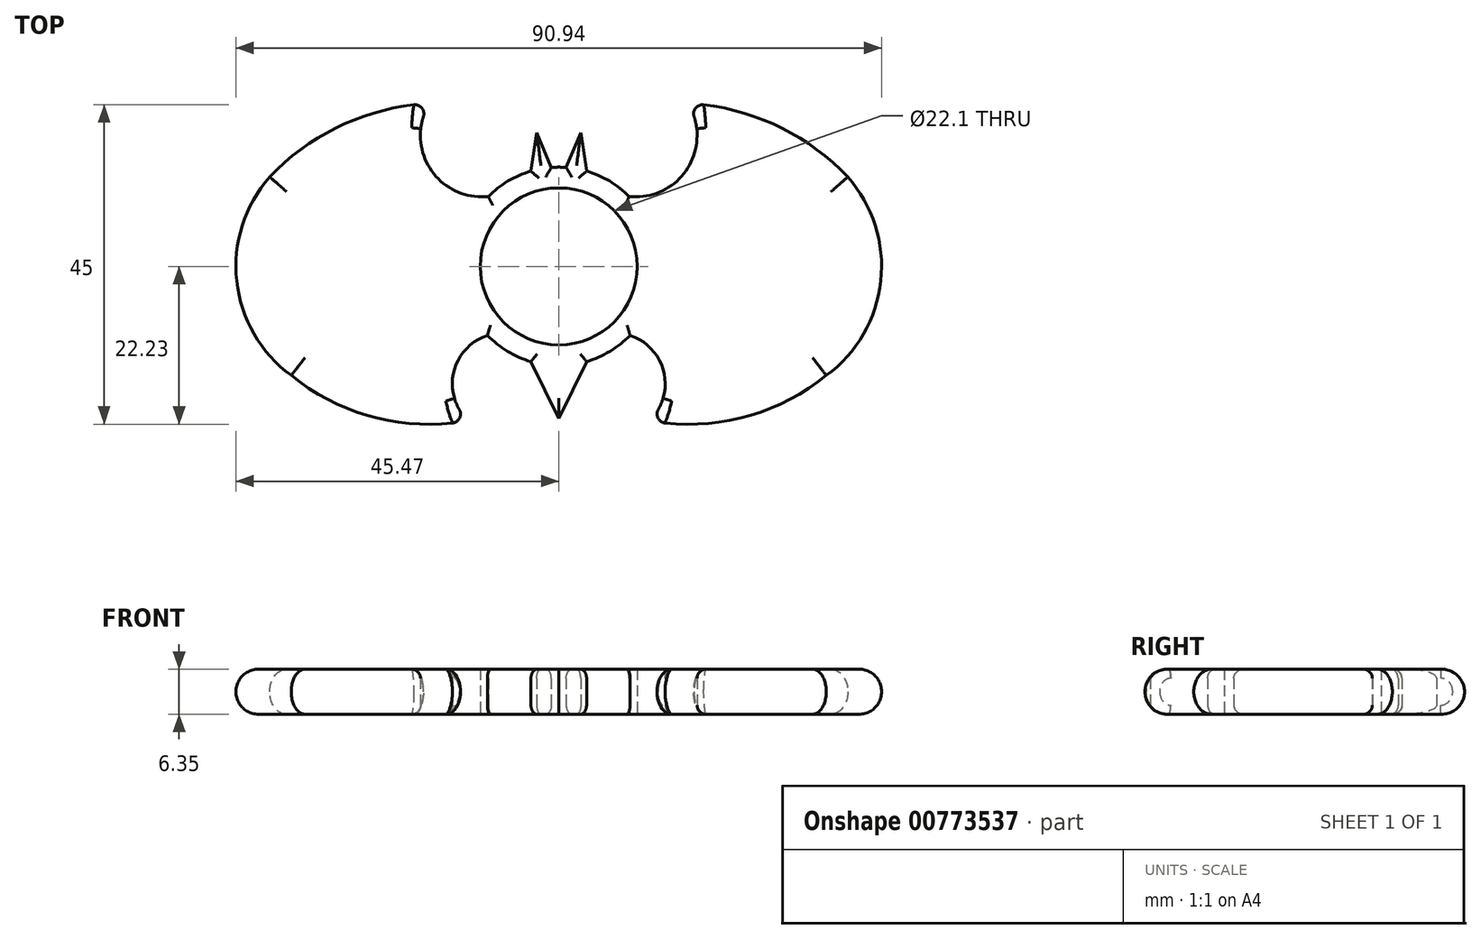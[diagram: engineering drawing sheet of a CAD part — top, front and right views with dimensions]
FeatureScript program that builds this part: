
annotation { "Feature Type Name" : "Feature", "Feature Type Description" : "" }
export const myFeature = defineFeature(function(context is Context, id is Id, definition is map)
    precondition{}
    {
        {
            var Q0;
            Q0=qCreatedBy(makeId("Top.planeOp"),FACE);
            var sketch = newSketch(context, id + "F0", { "sketchPlane" : qUnion([Q0])});
            skCircle(sketch, "E0", {"center": v(0, 0) * mm, "radius": 11.05 * mm});
            skCircle(sketch, "E1", {"center": v(0, 0) * mm, "radius": 13.97 * mm});
            skArc(sketch, "E2", {"start": v(37.68, -15.37) * mm, "mid": v(45.36, -2.05) * mm, "end": v(40.7, 12.6) * mm});
            skArc(sketch, "E3", {"start": v(-18.2, 22.95) * mm, "mid": v(-30.45, 19.93) * mm, "end": v(-40.7, 12.6) * mm});
            skArc(sketch, "E4", {"start": v(-18.2, 22.95) * mm, "mid": v(-18.15, 13.81) * mm, "end": v(-9.93, 9.83) * mm});
            skArc(sketch, "E5.trimOffspring", {"start": v(-40.7, 12.6) * mm, "mid": v(-45.36, -2.05) * mm, "end": v(-37.68, -15.37) * mm});
            skArc(sketch, "E6.MirrorCS", {"start": v(18.2, 22.95) * mm, "mid": v(18.15, 13.81) * mm, "end": v(9.93, 9.83) * mm});
            skArc(sketch, "E7.MirrorCS", {"start": v(18.2, 22.95) * mm, "mid": v(30.45, 19.93) * mm, "end": v(40.7, 12.6) * mm});
            skArc(sketch, "E8", {"start": v(-37.68, -15.37) * mm, "mid": v(-25.91, -21.27) * mm, "end": v(-12.76, -21.74) * mm});
            skArc(sketch, "E9", {"start": v(-10.03, -9.72) * mm, "mid": v(-14.81, -14.95) * mm, "end": v(-12.76, -21.74) * mm});
            skArc(sketch, "E10.MirrorCS", {"start": v(10.03, -9.72) * mm, "mid": v(14.81, -14.95) * mm, "end": v(12.76, -21.74) * mm});
            skArc(sketch, "E11.MirrorCS", {"start": v(37.68, -15.37) * mm, "mid": v(25.91, -21.27) * mm, "end": v(12.76, -21.74) * mm});
            skPoint(sketch, "E12.end.orphan", {"position": v(2.34, 18.82) * mm});
            skPoint(sketch, "E13.orphan", {"position": v(3.92, 13.4) * mm});
            skPoint(sketch, "E14.end.orphan", {"position": v(-1.04, 13.93) * mm});
            skPoint(sketch, "E15.end.orphan", {"position": v(-2.23, 18.82) * mm});
            skPoint(sketch, "E16.MirrorCS.end.orphan", {"position": v(1.04, 13.93) * mm});
            skPoint(sketch, "E16.MirrorCS.start.orphan", {"position": v(2.23, 18.82) * mm});
            skPoint(sketch, "E17.end.orphan", {"position": v(-4.8, 18.35) * mm});
            skPoint(sketch, "E18.MirrorCS.end.orphan", {"position": v(4.8, 18.35) * mm});
            skLineSegment(sketch, "E19", {"start": v(-1.04, 13.93) * mm, "end": v(-3.1, 18.83) * mm});
            skLineSegment(sketch, "E20", {"start": v(-3.1, 18.83) * mm, "end": v(-3.92, 13.4) * mm});
            skLineSegment(sketch, "E21.MirrorCS", {"start": v(1.04, 13.93) * mm, "end": v(3.1, 18.83) * mm});
            skLineSegment(sketch, "E22.MirrorCS", {"start": v(3.1, 18.83) * mm, "end": v(3.92, 13.4) * mm});
            skPoint(sketch, "E23.end.orphan", {"position": v(0, -21.45) * mm});
            skPoint(sketch, "E23.start.orphan", {"position": v(-4.01, -13.38) * mm});
            skPoint(sketch, "E24.MirrorCS.start.orphan", {"position": v(4.01, -13.38) * mm});
            skPoint(sketch, "E25.MirrorCS.end.orphan", {"position": v(-3.92, -13.4) * mm});
            skPoint(sketch, "E25.MirrorCS.start.orphan", {"position": v(-3.1, -18.83) * mm});
            skLineSegment(sketch, "E26", {"start": v(-3.92, -13.4) * mm, "end": v(0, -21.45) * mm});
            skLineSegment(sketch, "E27.MirrorCS", {"start": v(3.92, -13.4) * mm, "end": v(0, -21.45) * mm});
            skLineSegment(sketch, "E28", {"start": v(-26.42, 0) * mm, "end": v(-31.16, 0) * mm});
            skLineSegment(sketch, "E29", {"start": v(26.42, 0) * mm, "end": v(31.16, 0) * mm});
            skSolve(sketch);
        }
        {
            var Q0;
            Q0=qSketchRegion(id+"F0",true);
            extrude(context, id + "F1", {"entities" : qUnion([Q0]), "depth" : 6.35 * mm, "offsetDistance" : 25.4 * mm});
        }
        {
            var Q0;
            Q0=makeQuery(id+"F1.opExtrude","CAP_EDGE",EDGE,{"disambiguationData":[OSD([sQuery(id+"F0.wireOp",EDGE,"E5.trimOffspring")])],"isStart":false});
            var Q1;
            Q1=makeQuery(id+"F1.opExtrude","CAP_EDGE",EDGE,{"disambiguationData":[OSD([sQuery(id+"F0.wireOp",EDGE,"E2")])],"isStart":false});
            var Q2;
            Q2=makeQuery(id+"F1.opExtrude","CAP_EDGE",EDGE,{"disambiguationData":[OSD([sQuery(id+"F0.wireOp",EDGE,"E2")])],"isStart":true});
            var Q3;
            Q3=makeQuery(id+"F1.opExtrude","CAP_EDGE",EDGE,{"disambiguationData":[OSD([sQuery(id+"F0.wireOp",EDGE,"E5.trimOffspring")])],"isStart":true});
            fillet(context, id + "F2", {"entities" : qUnion([Q0, Q1, Q2, Q3]), "radius" : 3.17 * mm, "tangentPropagation" : true, "allowEdgeOverflow" : false});
        }
        {
            var Q0;
            Q0=makeQuery(id+"F2.opFillet","BLEND_EDGE",EDGE,{"blendedFrom":[makeQuery(id+"F1.opExtrude","CAP_EDGE",EDGE,{"disambiguationData":[OSD([sQuery(id+"F0.wireOp",EDGE,"E5.trimOffspring")])],"isStart":false}),makeQuery(id+"F1.opExtrude","SWEPT_FACE",FACE,{"disambiguationData":[OSD([sQuery(id+"F0.wireOp",EDGE,"E4")])]})],"blendedInto":[makeQuery(id+"F1.opExtrude","SWEPT_FACE",FACE,{"disambiguationData":[OSD([sQuery(id+"F0.wireOp",EDGE,"E4")])]})]});
            var Q1;
            Q1=makeQuery(id+"F2.opFillet","BLEND_EDGE",EDGE,{"blendedFrom":[makeQuery(id+"F1.opExtrude","CAP_EDGE",EDGE,{"disambiguationData":[OSD([sQuery(id+"F0.wireOp",EDGE,"E5.trimOffspring")])],"isStart":true}),makeQuery(id+"F1.opExtrude","SWEPT_FACE",FACE,{"disambiguationData":[OSD([sQuery(id+"F0.wireOp",EDGE,"E4")])]})],"blendedInto":[makeQuery(id+"F1.opExtrude","SWEPT_FACE",FACE,{"disambiguationData":[OSD([sQuery(id+"F0.wireOp",EDGE,"E4")])]})]});
            var Q2;
            Q2=makeQuery(id+"F1.opExtrude","CAP_EDGE",EDGE,{"disambiguationData":[OSD([sQuery(id+"F0.wireOp",EDGE,"E9")])],"isStart":false});
            var Q3;
            Q3=makeQuery(id+"F1.opExtrude","CAP_EDGE",EDGE,{"disambiguationData":[OSD([sQuery(id+"F0.wireOp",EDGE,"E10.MirrorCS")])],"isStart":false});
            var Q4;
            Q4=makeQuery(id+"F1.opExtrude","CAP_EDGE",EDGE,{"disambiguationData":[OSD([sQuery(id+"F0.wireOp",EDGE,"E6.MirrorCS")])],"isStart":false});
            var Q5;
            {var subQ0=sQuery(id+"F0.wireOp",EDGE,"E1");Q5=makeQuery(id+"F1.opExtrude","CAP_EDGE",EDGE,{"disambiguationData":[OSD([subQ0]),TDD([makeQuery(id+"F0.imprint","IMPRINT",EDGE,{"disambiguationData":[TD([[makeQuery(id+"F0.imprint","INTERSECT",VERTEX,{"derivedFrom":[subQ0,sQuery(id+"F0.wireOp",EDGE,"E4")]}),1.0]])],"derivedFrom":subQ0})])],"isStart":false});}
            var Q6;
            Q6=makeQuery(id+"F1.opExtrude","CAP_EDGE",EDGE,{"disambiguationData":[OSD([sQuery(id+"F0.wireOp",EDGE,"E20")])],"isStart":false});
            var Q7;
            {var subQ0=sQuery(id+"F0.wireOp",EDGE,"E1");Q7=makeQuery(id+"F1.opExtrude","CAP_EDGE",EDGE,{"disambiguationData":[OSD([subQ0]),TDD([makeQuery(id+"F0.imprint","IMPRINT",EDGE,{"disambiguationData":[TD([[makeQuery(id+"F0.imprint","INTERSECT",VERTEX,{"derivedFrom":[subQ0,sQuery(id+"F0.wireOp",EDGE,"E19")]}),1.0]])],"derivedFrom":subQ0})])],"isStart":false});}
            var Q8;
            Q8=makeQuery(id+"F1.opExtrude","CAP_EDGE",EDGE,{"disambiguationData":[OSD([sQuery(id+"F0.wireOp",EDGE,"E21.MirrorCS")])],"isStart":false});
            var Q9;
            {var subQ0=sQuery(id+"F0.wireOp",EDGE,"E1");Q9=makeQuery(id+"F1.opExtrude","CAP_EDGE",EDGE,{"disambiguationData":[OSD([subQ0]),TDD([makeQuery(id+"F0.imprint","IMPRINT",EDGE,{"disambiguationData":[TD([[makeQuery(id+"F0.imprint","INTERSECT",VERTEX,{"derivedFrom":[subQ0,sQuery(id+"F0.wireOp",EDGE,"E6.MirrorCS")]}),-1.0]])],"derivedFrom":subQ0})])],"isStart":false});}
            var Q10;
            {var subQ0=sQuery(id+"F0.wireOp",EDGE,"E1");Q10=makeQuery(id+"F1.opExtrude","CAP_EDGE",EDGE,{"disambiguationData":[OSD([subQ0]),TDD([makeQuery(id+"F0.imprint","IMPRINT",EDGE,{"disambiguationData":[TD([[makeQuery(id+"F0.imprint","INTERSECT",VERTEX,{"derivedFrom":[subQ0,sQuery(id+"F0.wireOp",EDGE,"E6.MirrorCS")]}),-1.0]])],"derivedFrom":subQ0})])],"isStart":true});}
            var Q11;
            Q11=makeQuery(id+"F1.opExtrude","CAP_EDGE",EDGE,{"disambiguationData":[OSD([sQuery(id+"F0.wireOp",EDGE,"E22.MirrorCS")])],"isStart":true});
            var Q12;
            {var subQ0=sQuery(id+"F0.wireOp",EDGE,"E1");Q12=makeQuery(id+"F1.opExtrude","CAP_EDGE",EDGE,{"disambiguationData":[OSD([subQ0]),TDD([makeQuery(id+"F0.imprint","IMPRINT",EDGE,{"disambiguationData":[TD([[makeQuery(id+"F0.imprint","INTERSECT",VERTEX,{"derivedFrom":[subQ0,sQuery(id+"F0.wireOp",EDGE,"E19")]}),1.0]])],"derivedFrom":subQ0})])],"isStart":true});}
            var Q13;
            Q13=makeQuery(id+"F1.opExtrude","CAP_EDGE",EDGE,{"disambiguationData":[OSD([sQuery(id+"F0.wireOp",EDGE,"E19")])],"isStart":true});
            var Q14;
            Q14=makeQuery(id+"F1.opExtrude","CAP_EDGE",EDGE,{"disambiguationData":[OSD([sQuery(id+"F0.wireOp",EDGE,"E20")])],"isStart":true});
            var Q15;
            {var subQ0=sQuery(id+"F0.wireOp",EDGE,"E1");Q15=makeQuery(id+"F1.opExtrude","CAP_EDGE",EDGE,{"disambiguationData":[OSD([subQ0]),TDD([makeQuery(id+"F0.imprint","IMPRINT",EDGE,{"disambiguationData":[TD([[makeQuery(id+"F0.imprint","INTERSECT",VERTEX,{"derivedFrom":[subQ0,sQuery(id+"F0.wireOp",EDGE,"E4")]}),1.0]])],"derivedFrom":subQ0})])],"isStart":true});}
            var Q16;
            {var subQ0=sQuery(id+"F0.wireOp",EDGE,"E1");Q16=makeQuery(id+"F1.opExtrude","CAP_EDGE",EDGE,{"disambiguationData":[OSD([subQ0]),TDD([makeQuery(id+"F0.imprint","IMPRINT",EDGE,{"disambiguationData":[TD([[makeQuery(id+"F0.imprint","INTERSECT",VERTEX,{"derivedFrom":[subQ0,sQuery(id+"F0.wireOp",EDGE,"E9")]}),-1.0]])],"derivedFrom":subQ0})])],"isStart":false});}
            var Q17;
            Q17=makeQuery(id+"F1.opExtrude","CAP_EDGE",EDGE,{"disambiguationData":[OSD([sQuery(id+"F0.wireOp",EDGE,"E26")])],"isStart":false});
            var Q18;
            Q18=makeQuery(id+"F1.opExtrude","CAP_EDGE",EDGE,{"disambiguationData":[OSD([sQuery(id+"F0.wireOp",EDGE,"E27.MirrorCS")])],"isStart":false});
            var Q19;
            {var subQ0=sQuery(id+"F0.wireOp",EDGE,"E1");Q19=makeQuery(id+"F1.opExtrude","CAP_EDGE",EDGE,{"disambiguationData":[OSD([subQ0]),TDD([makeQuery(id+"F0.imprint","IMPRINT",EDGE,{"disambiguationData":[TD([[makeQuery(id+"F0.imprint","INTERSECT",VERTEX,{"derivedFrom":[subQ0,sQuery(id+"F0.wireOp",EDGE,"E10.MirrorCS")]}),1.0]])],"derivedFrom":subQ0})])],"isStart":false});}
            var Q20;
            {var subQ0=sQuery(id+"F0.wireOp",EDGE,"E1");Q20=makeQuery(id+"F1.opExtrude","CAP_EDGE",EDGE,{"disambiguationData":[OSD([subQ0]),TDD([makeQuery(id+"F0.imprint","IMPRINT",EDGE,{"disambiguationData":[TD([[makeQuery(id+"F0.imprint","INTERSECT",VERTEX,{"derivedFrom":[subQ0,sQuery(id+"F0.wireOp",EDGE,"E10.MirrorCS")]}),1.0]])],"derivedFrom":subQ0})])],"isStart":true});}
            var Q21;
            Q21=makeQuery(id+"F1.opExtrude","CAP_EDGE",EDGE,{"disambiguationData":[OSD([sQuery(id+"F0.wireOp",EDGE,"E27.MirrorCS")])],"isStart":true});
            var Q22;
            Q22=makeQuery(id+"F1.opExtrude","CAP_EDGE",EDGE,{"disambiguationData":[OSD([sQuery(id+"F0.wireOp",EDGE,"E26")])],"isStart":true});
            var Q23;
            {var subQ0=sQuery(id+"F0.wireOp",EDGE,"E1");Q23=makeQuery(id+"F1.opExtrude","CAP_EDGE",EDGE,{"disambiguationData":[OSD([subQ0]),TDD([makeQuery(id+"F0.imprint","IMPRINT",EDGE,{"disambiguationData":[TD([[makeQuery(id+"F0.imprint","INTERSECT",VERTEX,{"derivedFrom":[subQ0,sQuery(id+"F0.wireOp",EDGE,"E9")]}),-1.0]])],"derivedFrom":subQ0})])],"isStart":true});}
            var Q24;
            Q24=makeQuery(id+"F1.opExtrude","CAP_EDGE",EDGE,{"disambiguationData":[OSD([sQuery(id+"F0.wireOp",EDGE,"E21.MirrorCS")])],"isStart":true});
            var Q25;
            Q25=makeQuery(id+"F1.opExtrude","CAP_EDGE",EDGE,{"disambiguationData":[OSD([sQuery(id+"F0.wireOp",EDGE,"E22.MirrorCS")])],"isStart":false});
            var Q26;
            Q26=makeQuery(id+"F1.opExtrude","CAP_EDGE",EDGE,{"disambiguationData":[OSD([sQuery(id+"F0.wireOp",EDGE,"E19")])],"isStart":false});
            fillet(context, id + "F3", {"entities" : qUnion([Q0, Q1, Q2, Q3, Q4, Q5, Q6, Q7, Q8, Q9, Q10, Q11, Q12, Q13, Q14, Q15, Q16, Q17, Q18, Q19, Q20, Q21, Q22, Q23, Q24, Q25, Q26]), "radius" : 1.27 * mm, "tangentPropagation" : true, "allowEdgeOverflow" : false});
        }
    });
